# Revit family: Pavilion Round
name_source: partatom
category: Lighting Fixtures
units: mm (PartAtom-declared; Revit-internal decimal feet)

## family parameters
Cut with Voids When Loaded = No
Host = Face
Light Source = Yes
OmniClass Number = 23.80.70.14.21
OmniClass Title = Street and Roadway Lighting
Part Type = Normal
Room Calculation Point = No
Round Connector Dimension = Use Diameter
Shared = No

## types (5) — shared parameters
Apparent Load = 22 VA
Color Filter = 16777215
Default Elevation = 48 "
Description = Pavilion redefines the bollard category with state of the art design, performance, and technology.
Dimming Lamp Color Temperature Shift = <None>
Emit Shape Visible in Rendering = No
Emit from Circle Diameter = 5 "
Fixture Finish = Color : Light Gray
Lamp = LED
Light Engine = 22W (2000 nominal lm), 5000K, 70 CRI
Load Classification = Lighting
Manufacturer = KIM Lighting
Model = Pavilion Round
Photometric Note = More IES files download in the Photometric Web link
Power Factor = 1
Tilt Angle = 90.00°
URL = https://www.currentlighting.com
Voltage = 120 V
Watt = 22 W

## per-type parameters (varying)
| type | Distribution | Lens Material | Optics | Photometric Web File |
| PA7R-GC4-12L-020-5K7 | Type IV | Glass | Grill with clear vertical lens | PA7R-GC4-12L-020-5K7.IES |
| PA7R-GD5-12L-020-5K7 | Type V | White Glass | Grill with diffuse vertical lens | PA7R-GD5-12L-020-5K7.IES |
| PA7R-GC3-12L-020-5K7 | Type III | Glass | Grill with clear vertical lens | PA7R-GC3-12L-020-5K7.IES |
| PA7R-CL2-12L-020-5K7 | Type II | Glass | Clear Vertical Lens | PA7R-CL2-12L-020-5K7.IES |
| PA7R-CH1-12L-020-5K7 | Type I | Glass | Clear Horizontal Lens | PA7R-CH1-12L-020-5K7.IES |

## geometry (parser evidence)
native form markers: Blend x8, Sweep x4
no freeform markers — native parametric forms only
